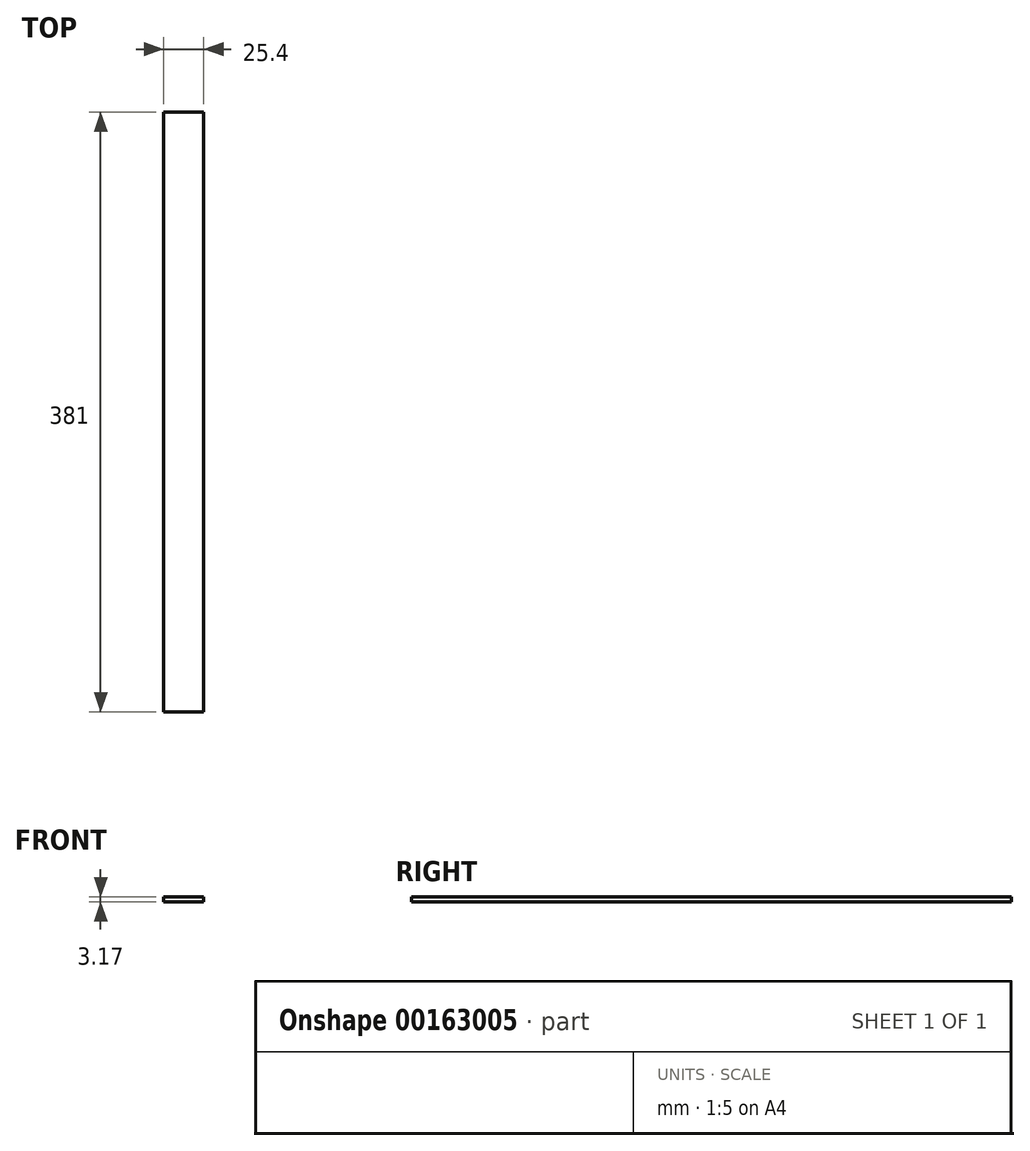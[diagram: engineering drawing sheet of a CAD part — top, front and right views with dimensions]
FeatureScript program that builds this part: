
annotation { "Feature Type Name" : "Feature", "Feature Type Description" : "" }
export const myFeature = defineFeature(function(context is Context, id is Id, definition is map)
    precondition{}
    {
        {
            var Q0;
            Q0=qCreatedBy(makeId("Top.planeOp"),FACE);
            var sketch = newSketch(context, id + "F0", { "sketchPlane" : qUnion([Q0])});
            skLineSegment(sketch, "E0.bottom", {"start": v(0, 0) * mm, "end": v(25.4, 0) * mm});
            skLineSegment(sketch, "E0.top", {"start": v(0, -381) * mm, "end": v(25.4, -381) * mm});
            skLineSegment(sketch, "E0.left", {"start": v(0, 0) * mm, "end": v(0, -381) * mm});
            skLineSegment(sketch, "E0.right", {"start": v(25.4, 0) * mm, "end": v(25.4, -381) * mm});
            skSolve(sketch);
        }
        {
            var Q0;
            Q0 = qSketchRegion(id + "F0", true);
            extrude(context, id + "F1", {"entities" : qUnion([Q0]), "depth" : 3.17 * mm});
        }
    });
